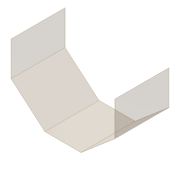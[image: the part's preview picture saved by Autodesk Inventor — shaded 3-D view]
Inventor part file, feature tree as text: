
AUTODESK INVENTOR PART (.ipt)
format: ipt  version: 2012 (Build 160160000, 160)  size: 84,480 bytes
history: native  units: in
note: dims shown in document units (in); Inventor stores cm internally (conversion verified against a paired STEP export)
features: extrude x1, sketch x1
ambient origin geometry x8: Origin, YZ Plane, XZ Plane, XY Plane, X Axis, Y Axis, Z Axis, Center Point
bodies: Solid1 (feature_tree)
feature tree (2):
  extrude  "Extrusion1"  Depth=0.0625in
  sketch  "Sketch1"  dims[d0=0.0625in d1=0.0625in d2=0.0625in d3=14.0in d4=23.0in d5=8.0in d6=12.0in d7=0.0in]
